# Revit family: Lighting_Fixture-Ceiling-Astro-Minima_LED
name_source: partatom
category: Lighting Fixtures
revit_build: Autodesk Revit 2014 (Build: 20130308_1515(x64)
units: mm (PartAtom-declared; Revit-internal decimal feet)

## types (1)
- 5701 Minima LED
    Apparent Load = 11 VA
    Assembly Code = D5020200
    Casing Material = Astro - Aluminium - White
    Class = 3
    Color Filter = 16777215
    Default Elevation = 1219.2 mm  [stored 4 ft]
    Description = Down Light
    Dimmable = Yes, if a dimmable driver is used.
    Dimming Lamp Color Temperature Shift = <None>
    Energy Efficiency Rating = A+
    Height = 97 mm  [stored 0.318241 ft]
    IP Rating = IP20
    Lamp = LED
    Lamp included = Yes
    Length = 82 mm  [stored 0.269029 ft]
    Light Source Elevation = 45 mm  [stored 0.147638 ft]
    Luminaire Lamp Efficiency Rating = A+
    Manufacturer = Astro Lighting Ltd, CM20 2DP
    Model = 5701 Minima LED
    Mountable on normally flammable surfaces = Yes
    Number of Poles = 1
    Photometric Web File = 5701 MINIMA LED FIXED.ies
    Product Documentation = http://www.astrolighting.co.uk
    Suitable for bathroom zone = Zone 3
    Tilt Angle = -90.00°
    Type Comments = - Requires a 700mA constant current LED driver. -This product can be dimmed if a dimmable driver is used. -Requires a 77mm cut out hole
    URL = www.astrolighting.co.uk
    Voltage = 230 V
    Wattage Comments = 7.4w
    Weight = 0.25kg
    Width = 82 mm  [stored 0.269029 ft]

note: [stored X ft] marks values corroborated as IEEE doubles in the binary element streams (Revit-internal decimal feet)

## geometry (parser evidence)
native form markers: Sweep x1
no freeform markers — native parametric forms only
